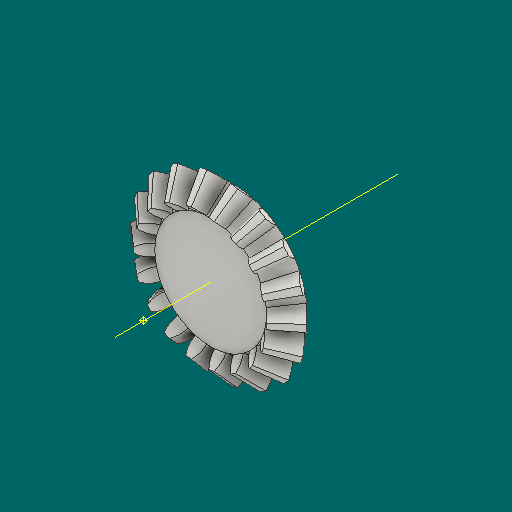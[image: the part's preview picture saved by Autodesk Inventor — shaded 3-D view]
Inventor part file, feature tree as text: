
AUTODESK INVENTOR PART (.ipt)
format: ipt  version: 2023.1 (Build 271208000, 208)  size: 487,424 bytes
history: native  units: mm
features: other x24, loft x2, pattern_circular x2, sketch x1
ambient origin geometry x6: Origin, XZ Plane, X Axis, Y Axis, Z Axis, Center Point
bodies: Solid1 (feature_tree)
feature tree (29):
  other  "Top Point"
  other  "Mesh Plane2"
  other  "Teeth Body"
  other  "Start Point"
  other  "Tooth Plane"
  other  "Start Sketch"
  other  "End Point"
  other  "3D Sketch Right"
  other  "End Plane Right"
  loft  "Loft Right"
  pattern_circular  "Circular Pattern Right"  [2 undecoded]
  other  "3D Sketch Left"
  other  "End Plane Left"
  loft  "Loft Left"
  pattern_circular  "Circular Pattern Left"  [2 undecoded]
  other  "Fix Body"
  other  "Mesh Plane"
  other  "Top Plane"
  other  "Teeth Body Sketch"
  other  "End Plane"
  other  "End Sketch"
  other  "Helical Curve Left"
  other  "End Sketch Left"
  other  "Body Sketch"
  sketch  "Sketch6"  dims[d0=22.86mm d1=20.704739mm d2=24.656051mm d3=4.0mm d4=10.531974mm d5=90.0deg d7=4.61849mm d8=5.357012mm d9=14.610805mm d11=4.1397mm d12=3.4357mm d15=3.985088mm d16=10.868995mm d17=0.0mm d18=90.0deg d19=0.0mm d20=90.0deg d21=180.0mm d22=360.0deg d26=70.487871mm d27=2.92721mm d28=22.86mm d29=-7.853982mm d30=3.4357mm d31=3.985088mm d32=10.868995mm d35=0.0mm d37=0.0mm d39=0.0mm d40=90.0deg d41=180.0mm d42=360.0deg d46=90.0deg d47=90.0deg d48=0.0mm d49=0.0mm d50=90.0deg d51=1.745329mm d52=0.0mm d53=0.0mm d54=0.0mm d56=6.529237mm d57=18.272661mm d58=14.305181mm d59=13.593054mm d60=10.641641mm d61=13.593054mm d62=10.641641mm d63=90.0deg d64=90.0deg d65=70.487871mm d66=31.5mm d67=22.86mm d68=-7.853982mm d69=2.92721mm d70=3.985088mm d71=10.868995mm d72=3.4357mm d73=10.641641mm d74=13.593054mm d75=0.0mm d76=90.0deg d77=0.0mm d78=90.0deg d79=0.0mm d80=90.0deg d81=180.0mm d82=360.0deg d84=10.0mm d85=20.0mm d86=20.0mm d87=10.0mm d88=0.0mm d89=0.0mm]
  other  "Srf1"
  other  "Helical Curve Right"
  other  "End Sketch Right"
  other  "Pitch Diameter"
note: 4 required parameter values undecoded (feature->parameter linkage not recoverable at this tier; creation-order binding heuristic only, values carry confidence <= 0.55)
